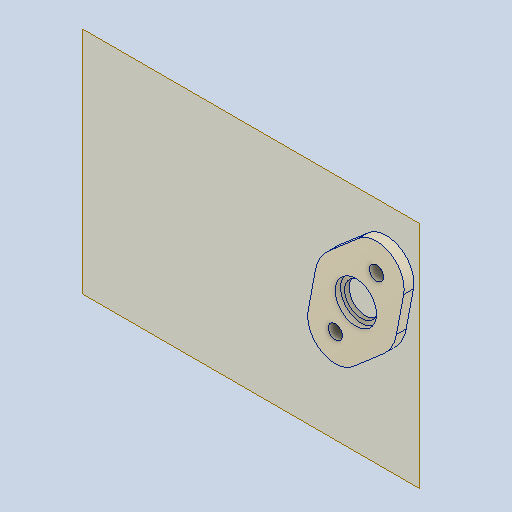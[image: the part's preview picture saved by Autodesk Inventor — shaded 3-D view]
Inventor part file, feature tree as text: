
AUTODESK INVENTOR PART (.ipt)
format: ipt  version: 2023 (Build 270158000, 158)  size: 128,512 bytes
history: native  units: in
note: dims shown in document units (in); Inventor stores cm internally (conversion verified against a paired STEP export)
features: other x3, sketch x2, plane x1
ambient origin geometry x8: Origin, YZ Plane, XZ Plane, XY Plane, X Axis, Y Axis, Z Axis, Center Point
bodies: Solid1 (feature_tree)
feature tree (6):
  other  "IntakeBearingBlock.ipt"
  other  "Solid1::IntakeBearingBlock.ipt"
  other  "TaggingFeature1"
  sketch  "Sketch1"  dims[d0=0.3937in]
  sketch  "Sketch2"
  plane  "Work Plane1"
